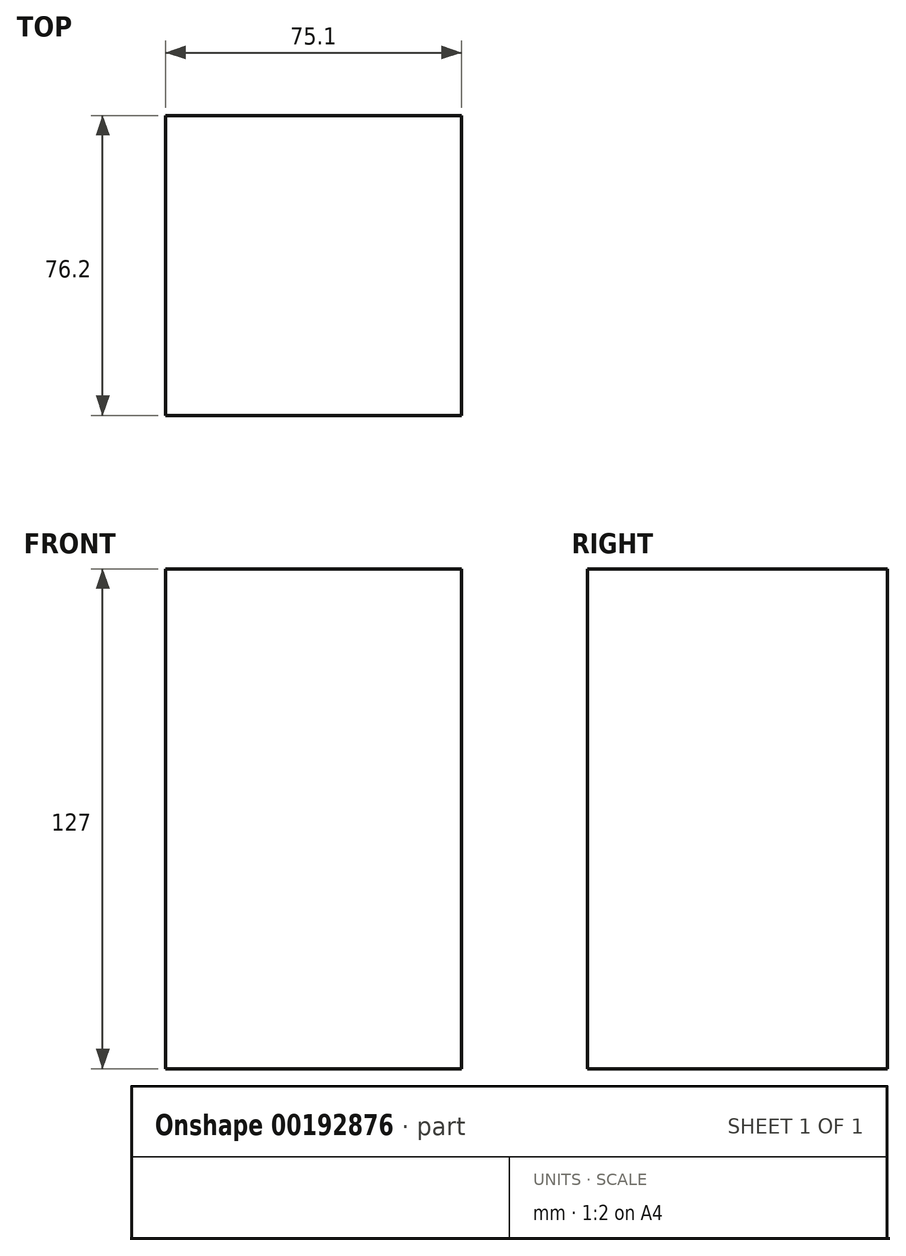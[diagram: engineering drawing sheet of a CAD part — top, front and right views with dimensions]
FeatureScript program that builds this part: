
annotation { "Feature Type Name" : "Feature", "Feature Type Description" : "" }
export const myFeature = defineFeature(function(context is Context, id is Id, definition is map)
    precondition{}
    {
        {
            var Q0;
            Q0=qCreatedBy(makeId("Top.planeOp"),FACE);
            var sketch = newSketch(context, id + "F0", { "sketchPlane" : qUnion([Q0])});
            skLineSegment(sketch, "E0.bottom", {"start": v(37.55, 38.1) * mm, "end": v(-37.55, 38.1) * mm});
            skLineSegment(sketch, "E0.top", {"start": v(37.55, -38.1) * mm, "end": v(-37.55, -38.1) * mm});
            skLineSegment(sketch, "E0.left", {"start": v(37.55, 38.1) * mm, "end": v(37.55, -38.1) * mm});
            skLineSegment(sketch, "E0.right", {"start": v(-37.55, 38.1) * mm, "end": v(-37.55, -38.1) * mm});
            skPoint(sketch, "E0.middle", {"position": v(0, 0) * mm});
            skSolve(sketch);
        }
        {
            var Q0;
            Q0=makeQuery(id+"F0.imprint","IMPRINT",FACE,{"disambiguationData":[TD([[makeQuery(id+"F0.imprint","IMPRINT",EDGE,{"derivedFrom":sQuery(id+"F0.wireOp",EDGE,"E0.bottom")}),1.0]])]});
            extrude(context, id + "F1", {"entities" : qUnion([Q0]), "depth" : 127 * mm});
        }
    });
